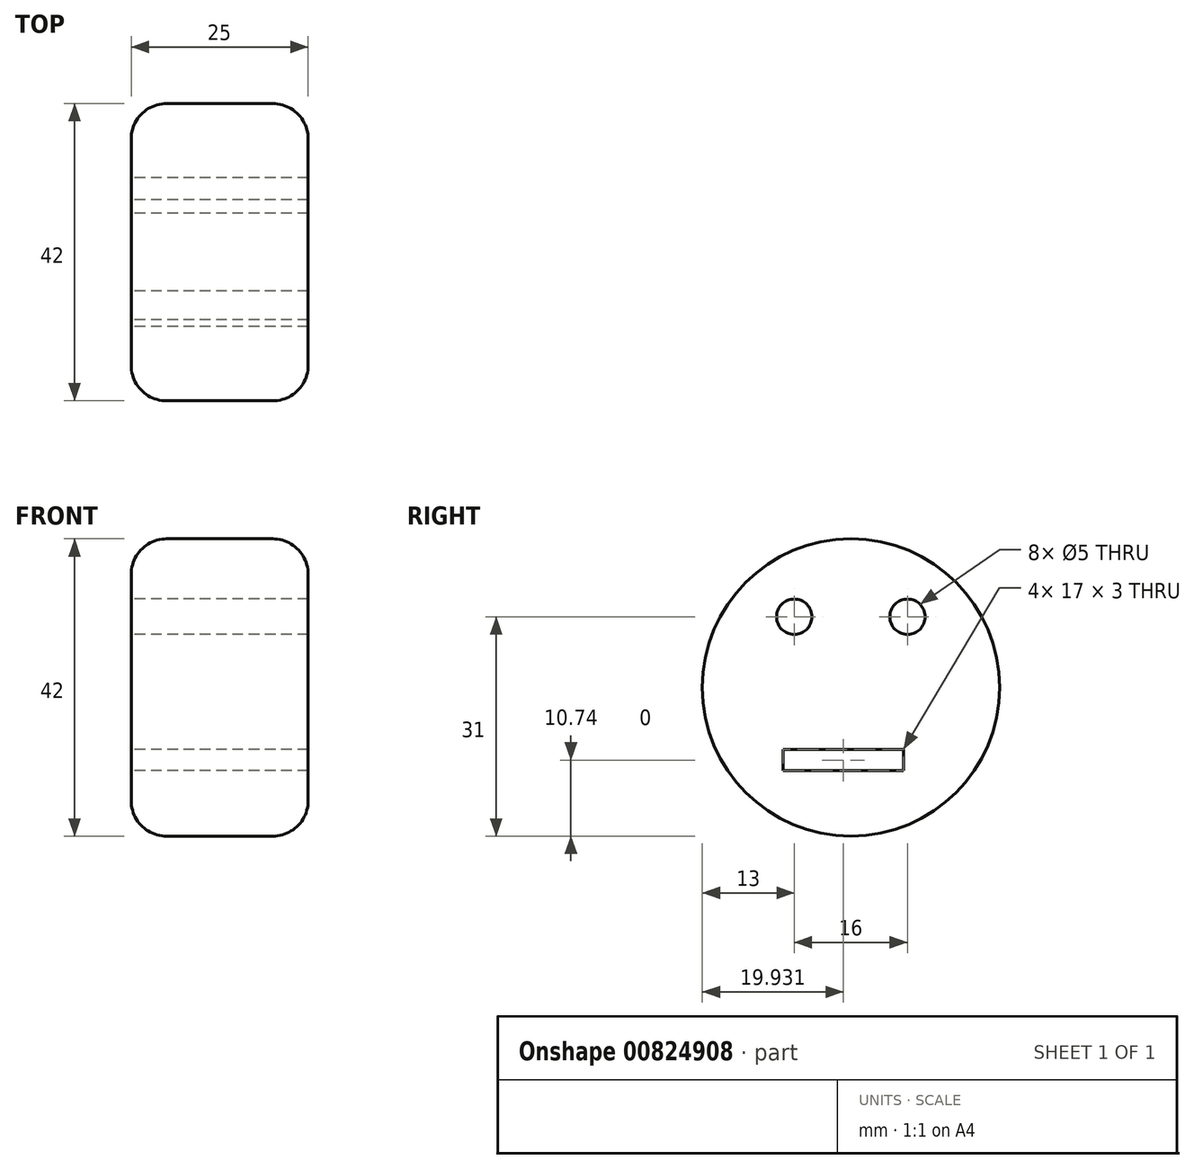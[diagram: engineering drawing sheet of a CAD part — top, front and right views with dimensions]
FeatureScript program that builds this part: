
annotation { "Feature Type Name" : "Feature", "Feature Type Description" : "" }
export const myFeature = defineFeature(function(context is Context, id is Id, definition is map)
    precondition{}
    {
        {
            var Q0;
            Q0=qCreatedBy(makeId("Right.planeOp"),FACE);
            var sketch = newSketch(context, id + "F0", { "sketchPlane" : qUnion([Q0])});
            skCircle(sketch, "E0", {"center": v(0, 0) * mm, "radius": 21 * mm});
            skCircle(sketch, "E1", {"center": v(-8, 10) * mm, "radius": 2.5 * mm});
            skCircle(sketch, "E2", {"center": v(8, 10) * mm, "radius": 2.5 * mm});
            skLineSegment(sketch, "E3", {"start": v(-9.57, -8.76) * mm, "end": v(7.43, -8.76) * mm});
            skLineSegment(sketch, "E4", {"start": v(7.43, -8.76) * mm, "end": v(7.43, -11.76) * mm});
            skLineSegment(sketch, "E5", {"start": v(7.43, -11.76) * mm, "end": v(-9.57, -11.76) * mm});
            skLineSegment(sketch, "E6", {"start": v(-9.57, -11.76) * mm, "end": v(-9.57, -8.76) * mm});
            skSolve(sketch);
        }
        {
            var Q0;
            Q0 = qSketchRegion(id + "F0", true);
            var Q1;
            Q1=makeQuery(id+"F0.imprint","IMPRINT",FACE,{"disambiguationData":[TD([[makeQuery(id+"F0.imprint","IMPRINT",EDGE,{"derivedFrom":sQuery(id+"F0.wireOp",EDGE,"E0")}),1.0]])]});
            extrude(context, id + "F1", {"entities" : qUnion([Q0, Q1]), "depth" : 25 * mm, "offsetDistance" : 25 * mm});
        }
        {
            var Q0;
            Q0=makeQuery(id+"F1.opExtrude","CAP_EDGE",EDGE,{"disambiguationData":[OSD([sQuery(id+"F0.wireOp",EDGE,"E0")])],"isStart":false});
            var Q1;
            Q1=makeQuery(id+"F1.opExtrude","CAP_EDGE",EDGE,{"disambiguationData":[OSD([sQuery(id+"F0.wireOp",EDGE,"E0")])],"isStart":true});
            fillet(context, id + "F2", {"entities" : qUnion([Q0, Q1]), "radius" : 5 * mm, "tangentPropagation" : true, "allowEdgeOverflow" : false});
        }
    });
